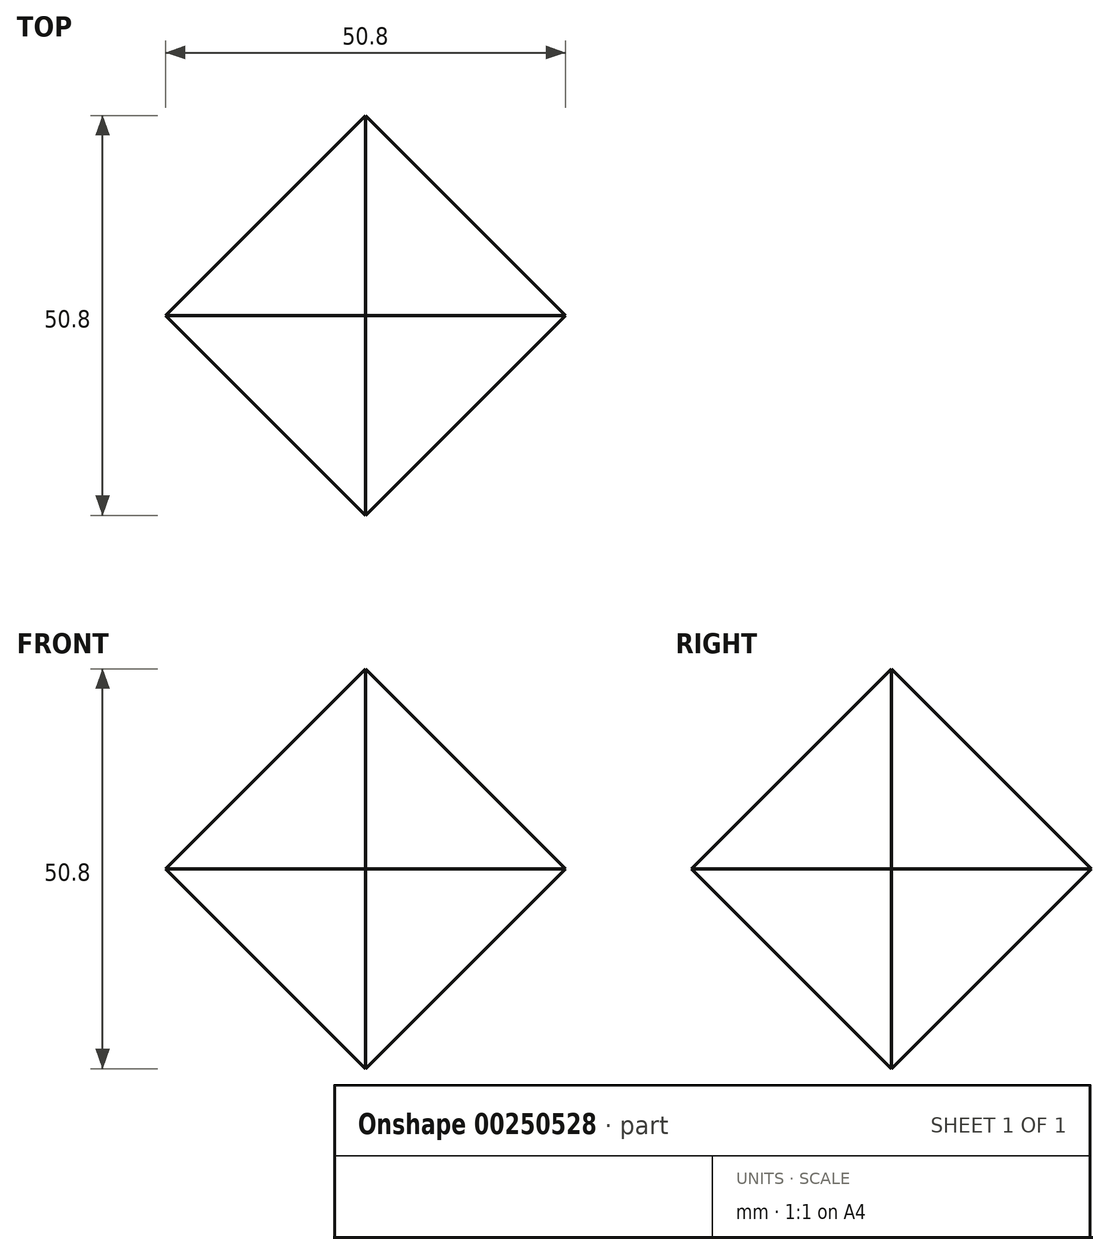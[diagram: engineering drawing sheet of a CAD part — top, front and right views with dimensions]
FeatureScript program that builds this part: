
annotation { "Feature Type Name" : "Feature", "Feature Type Description" : "" }
export const myFeature = defineFeature(function(context is Context, id is Id, definition is map)
    precondition{}
    {
        {
            var Q0;
            Q0=qCreatedBy(makeId("Front.planeOp"),FACE);
            var sketch = newSketch(context, id + "F0", { "sketchPlane" : qUnion([Q0])});
            skLineSegment(sketch, "E0.bottom", {"start": v(25.4, 25.4) * mm, "end": v(-25.4, 25.4) * mm});
            skLineSegment(sketch, "E0.top", {"start": v(25.4, -25.4) * mm, "end": v(-25.4, -25.4) * mm});
            skLineSegment(sketch, "E0.left", {"start": v(25.4, 25.4) * mm, "end": v(25.4, -25.4) * mm});
            skLineSegment(sketch, "E0.right", {"start": v(-25.4, 25.4) * mm, "end": v(-25.4, -25.4) * mm});
            skPoint(sketch, "E0.middle", {"position": v(0, 0) * mm});
            skSolve(sketch);
        }
        {
            var Q0;
            Q0 = qSketchRegion(id + "F0", true);
            extrude(context, id + "F1", {"entities" : qUnion([Q0]), "endBound" : BoundingType.SYMMETRIC, "depth" : 50.8 * mm});
        }
        {
            var Q0;
            Q0=makeQuery(id+"F1.opExtrude","SWEPT_FACE",FACE,{"disambiguationData":[OSD([sQuery(id+"F0.wireOp",EDGE,"E0.top")])]});
            var Q1;
            Q1=makeQuery(id+"F1.opExtrude","CAP_FACE",FACE,{"disambiguationData":[OSD([sQuery(id+"F0.wireOp",EDGE,"E0.bottom"),sQuery(id+"F0.wireOp",EDGE,"E0.top"),sQuery(id+"F0.wireOp",EDGE,"E0.left"),sQuery(id+"F0.wireOp",EDGE,"E0.right")])],"isStart":true});
            var Q2;
            Q2=makeQuery(id+"F1.opExtrude","SWEPT_FACE",FACE,{"disambiguationData":[OSD([sQuery(id+"F0.wireOp",EDGE,"E0.left")])]});
            var Q3;
            Q3=makeQuery(id+"F1.opExtrude","CAP_FACE",FACE,{"disambiguationData":[OSD([sQuery(id+"F0.wireOp",EDGE,"E0.bottom"),sQuery(id+"F0.wireOp",EDGE,"E0.top"),sQuery(id+"F0.wireOp",EDGE,"E0.left"),sQuery(id+"F0.wireOp",EDGE,"E0.right")])],"isStart":false});
            var Q4;
            Q4=makeQuery(id+"F1.opExtrude","SWEPT_FACE",FACE,{"disambiguationData":[OSD([sQuery(id+"F0.wireOp",EDGE,"E0.bottom")])]});
            chamfer(context, id + "F2", {"entities" : qUnion([Q0, Q1, Q2, Q3, Q4]), "width" : 25.4 * mm, "tangentPropagation" : true});
        }
    });
